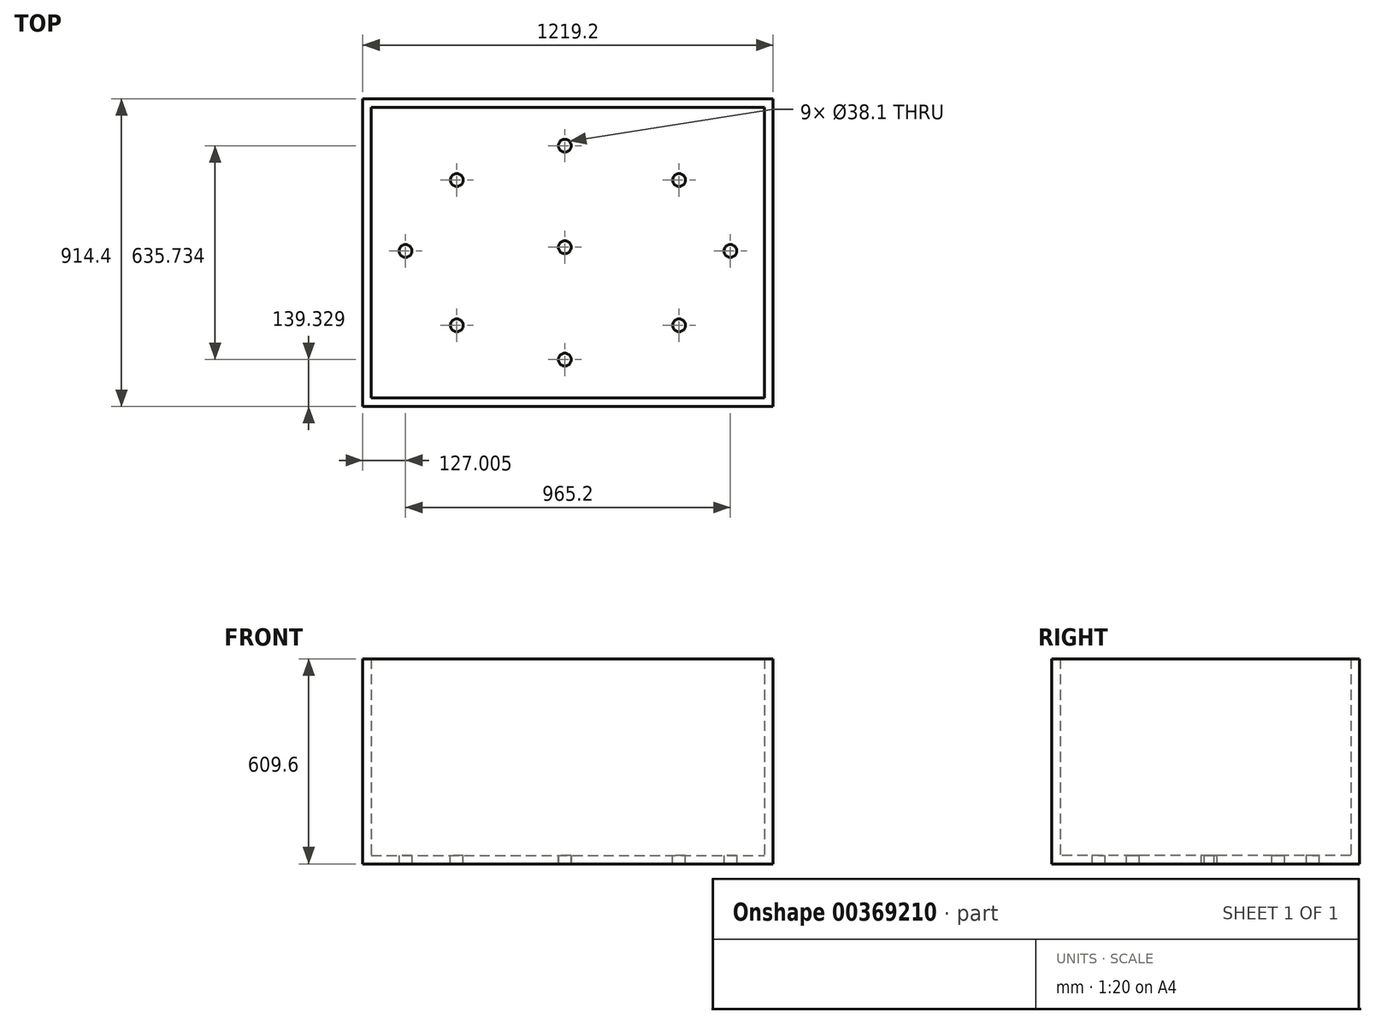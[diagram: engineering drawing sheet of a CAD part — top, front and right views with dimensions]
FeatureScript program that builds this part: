
annotation { "Feature Type Name" : "Feature", "Feature Type Description" : "" }
export const myFeature = defineFeature(function(context is Context, id is Id, definition is map)
    precondition{}
    {
        {
            var Q0;
            Q0=qCreatedBy(makeId("Top.planeOp"),FACE);
            var sketch = newSketch(context, id + "F0", { "sketchPlane" : qUnion([Q0])});
            skLineSegment(sketch, "E0.bottom", {"start": v(-600.45, 351.23) * mm, "end": v(618.75, 351.23) * mm});
            skLineSegment(sketch, "E0.top", {"start": v(-600.45, -563.17) * mm, "end": v(618.75, -563.17) * mm});
            skLineSegment(sketch, "E0.left", {"start": v(-600.45, 351.23) * mm, "end": v(-600.45, -563.17) * mm});
            skLineSegment(sketch, "E0.right", {"start": v(618.75, 351.23) * mm, "end": v(618.75, -563.17) * mm});
            skSolve(sketch);
        }
        {
            var Q0;
            Q0 = qSketchRegion(id + "F0", true);
            extrude(context, id + "F1", {"entities" : qUnion([Q0]), "depth" : 609.6 * mm});
        }
        {
            var Q0;
            Q0=makeQuery(id+"F1.opExtrude","CAP_FACE",FACE,{"disambiguationData":[OSD([sQuery(id+"F0.wireOp",EDGE,"E0.bottom"),sQuery(id+"F0.wireOp",EDGE,"E0.top"),sQuery(id+"F0.wireOp",EDGE,"E0.left"),sQuery(id+"F0.wireOp",EDGE,"E0.right")])],"isStart":false});
            shell(context, id + "F2", {"entities" : qUnion([Q0]), "thickness" : 25.4 * mm});
        }
        {
            var Q0;
            Q0=makeQuery(id+"F2.opShell","OFFSET_FACE",FACE,{"disambiguationData":[OSD([sQuery(id+"F0.wireOp",EDGE,"E0.bottom"),sQuery(id+"F0.wireOp",EDGE,"E0.top"),sQuery(id+"F0.wireOp",EDGE,"E0.left"),sQuery(id+"F0.wireOp",EDGE,"E0.right")])]});
            var sketch = newSketch(context, id + "F3", { "sketchPlane" : qUnion([Q0])});
            skPoint(sketch, "E1", {"position": v(-321.05, -321.87) * mm});
            skPoint(sketch, "E2", {"position": v(-321.05, 109.93) * mm});
            skPoint(sketch, "E3", {"position": v(339.35, 109.93) * mm});
            skPoint(sketch, "E4", {"position": v(339.35, -321.87) * mm});
            skPoint(sketch, "E5", {"position": v(0, -89.65) * mm});
            skSolve(sketch);
        }
        {
            var Q0;
            Q0=sQuery(id+"F3.wireOp",VERTEX,"E2");
            var Q1;
            Q1=sQuery(id+"F3.wireOp",VERTEX,"E3");
            var Q2;
            Q2=sQuery(id+"F3.wireOp",VERTEX,"E4");
            var Q3;
            Q3=sQuery(id+"F3.wireOp",VERTEX,"E1");
            var Q4;
            Q4=sQuery(id+"F3.wireOp",VERTEX,"E5");
            var Q5;
            Q5=makeQuery(id+"F1.opExtrude","SWEPT_BODY",BODY,{"disambiguationData":[OSD([sQuery(id+"F0.wireOp",EDGE,"E0.bottom"),sQuery(id+"F0.wireOp",EDGE,"E0.top"),sQuery(id+"F0.wireOp",EDGE,"E0.left"),sQuery(id+"F0.wireOp",EDGE,"E0.right")])]});
            hole(context, id + "F4", {"style" : HoleStyle.SIMPLE, "endStyle" : HoleEndStyle.THROUGH, "holeDiameter" : 38.1 * mm, "isTappedThrough" : true, "tappedDepth" : 12.7 * mm, "tapClearance" : 3, "locations" : qUnion([Q0, Q1, Q2, Q3, Q4]), "scope" : qUnion([Q5])});
        }
        {
            var Q0;
            Q0=qCreatedBy(makeId("Top.planeOp"),FACE);
            var sketch = newSketch(context, id + "F5", { "sketchPlane" : qUnion([Q0])});
            skPoint(sketch, "E6", {"position": v(0, 211.9) * mm});
            skPoint(sketch, "E7", {"position": v(0, -423.84) * mm});
            skSolve(sketch);
        }
        {
            var Q0;
            Q0=sQuery(id+"F5.wireOp",VERTEX,"E6");
            var Q1;
            Q1=sQuery(id+"F5.wireOp",VERTEX,"E7");
            var Q2;
            Q2=makeQuery(id+"F1.opExtrude","SWEPT_BODY",BODY,{"disambiguationData":[OSD([sQuery(id+"F0.wireOp",EDGE,"E0.bottom"),sQuery(id+"F0.wireOp",EDGE,"E0.top"),sQuery(id+"F0.wireOp",EDGE,"E0.left"),sQuery(id+"F0.wireOp",EDGE,"E0.right")])]});
            hole(context, id + "F6", {"style" : HoleStyle.SIMPLE, "endStyle" : HoleEndStyle.THROUGH, "oppositeDirection" : true, "holeDiameter" : 38.1 * mm, "isTappedThrough" : true, "tappedDepth" : 12.7 * mm, "tapClearance" : 3, "locations" : qUnion([Q0, Q1]), "scope" : qUnion([Q2])});
        }
        {
            var Q0;
            Q0=qCreatedBy(makeId("Top.planeOp"),FACE);
            var sketch = newSketch(context, id + "F7", { "sketchPlane" : qUnion([Q0])});
            skPoint(sketch, "E8", {"position": v(491.75, -100.9) * mm});
            skPoint(sketch, "E9", {"position": v(-669.69, -100.9) * mm});
            skPoint(sketch, "E10", {"position": v(-473.45, -100.9) * mm});
            skPoint(sketch, "E11", {"position": v(-673.7, -111.94) * mm});
            skSolve(sketch);
        }
        {
            var Q0;
            Q0=sQuery(id+"F7.wireOp",VERTEX,"E10");
            var Q1;
            Q1=sQuery(id+"F7.wireOp",VERTEX,"E8");
            var Q2;
            Q2=makeQuery(id+"F1.opExtrude","SWEPT_BODY",BODY,{"disambiguationData":[OSD([sQuery(id+"F0.wireOp",EDGE,"E0.bottom"),sQuery(id+"F0.wireOp",EDGE,"E0.top"),sQuery(id+"F0.wireOp",EDGE,"E0.left"),sQuery(id+"F0.wireOp",EDGE,"E0.right")])]});
            hole(context, id + "F8", {"style" : HoleStyle.SIMPLE, "endStyle" : HoleEndStyle.THROUGH, "oppositeDirection" : true, "holeDiameter" : 38.1 * mm, "isTappedThrough" : true, "tappedDepth" : 12.7 * mm, "tapClearance" : 3, "locations" : qUnion([Q0, Q1]), "scope" : qUnion([Q2])});
        }
    });
